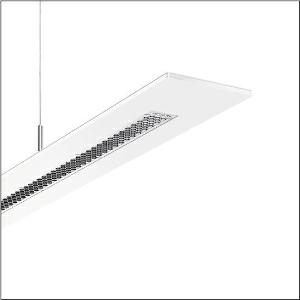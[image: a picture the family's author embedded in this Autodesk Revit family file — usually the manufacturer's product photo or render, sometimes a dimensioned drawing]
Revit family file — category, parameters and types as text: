
# Revit family: arktika_r__21_duo_5mb252dl60830_d82e
name_source: partatom
category: Lighting Fixtures
units: mm (PartAtom-declared; Revit-internal decimal feet)

## family parameters
Cut with Voids When Loaded = No
Host = Face
Light Source = No
Part Type = Normal
Room Calculation Point = No
Round Connector Dimension = Use Diameter
Shared = No

## types (1)
- --- (1 x LED 3000K / CRI = 80 (unbekannt), 8100 lm, 3000K)
    Apparent Load = 67 VA
    CIE Flux Codes = 81 100 100 79 100
    Color Rendering = 80
    Color Temperature = 3000K
    Default Elevation = 1800 mm
    Description = Arktika® 21 duo, office luminaire, primary anti-glare with honeycomb louvre, of plastic, aluminium vaporised, highly specular, light emission: direct/indirect distribution, primary light characteristic: symmetric, installation type: suspended mounting, LED, rated luminous flux: 8.100lm, luminous efficacy: 122lm/W, light colour: 830, colour temperature: 3000K, control gear: ECG DALI, with terminal, 3+2-pole, max. 2.5mm², mains connection: 220..240V, AC, 50/60Hz, rated input power: 67W, housing, of aluminium, powder-coated, traffic white (RAL 9016), 2-length, length: 2.280mm, width: 120mm, height: 8mm, protection rating (complete): IP20, insulation class (complete): insulation class II (safety insulation), certification: CE, packaging unit: 1 piece
    Height = 8 mm  [stored 0.0262467 ft]
    Lamp = 1 x LED 3000K / CRI >= 80 (unbekannt)
    Lamp Light Flux = 8100 lm
    Lamp count = 1
    Length = 2280 mm
    Luminous efficacy = 122 lm/W
    Manufacturer = Siteco
    ModVariant = No
    Model = 5MB252DL60830
    Mounting Place = Ceiling
    Mounting Type = Pendant
    Number of Poles = 1
    OnlyDefault = Yes
    Power Factor = 1
    Product Name = Arktika® 21 duo
    Product group = office luminaire | ceiling pendant
    ProductGroupID = 902
    Protection Class = Protection class II
    Protection Degree = IP 20
    RLX_Detail_Level = 1
    RLX_Emergency_Light_Flux = 0 lm
    RLX_Emergency_Type = 0
    RLX_Emergency_Type_DB = No
    RlxData = <blob elided: 39733 chars, md5=dbb78ba9>
    Socket = socket
    Standby Power = 0 W
    System Light Flux = 8100 lm
    System Power = 67 W
    Type Comments = factory setting: luminous flux: 100 % | dim-lin: 254 | 1330 mA
    Type Image = l_1006128.jpg
    URL = http://relux.com
    VarID = @adj_164517
    Voltage = 0 V
    Weight = 0.00 kg
    Width = 120 mm

note: [stored X ft] marks values corroborated as IEEE doubles in the binary element streams (Revit-internal decimal feet)

## geometry (parser evidence)
native form markers: Blend x4, Sweep x11
no freeform markers — native parametric forms only
